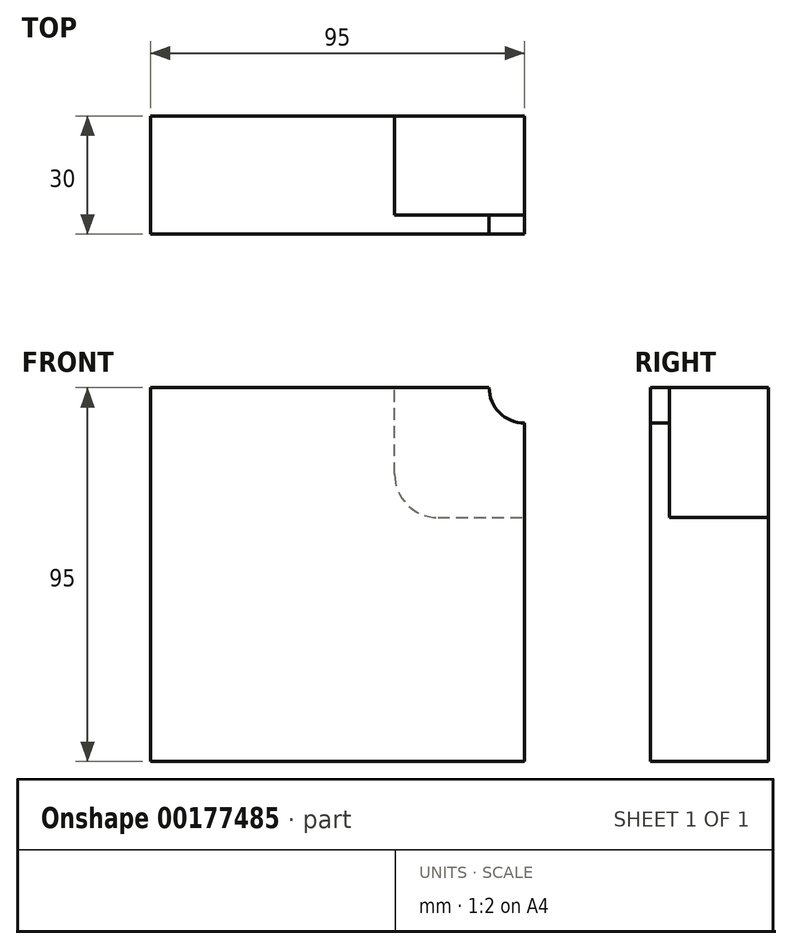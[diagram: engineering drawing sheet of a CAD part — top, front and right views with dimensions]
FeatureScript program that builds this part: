
annotation { "Feature Type Name" : "Feature", "Feature Type Description" : "" }
export const myFeature = defineFeature(function(context is Context, id is Id, definition is map)
    precondition{}
    {
        {
            var Q0;
            Q0=qCreatedBy(makeId("Front.planeOp"),FACE);
            var sketch = newSketch(context, id + "F0", { "sketchPlane" : qUnion([Q0])});
            skLineSegment(sketch, "E0.bottom", {"start": v(47.5, -47.5) * mm, "end": v(-47.5, -47.5) * mm});
            skLineSegment(sketch, "E0.top", {"start": v(47.5, 47.5) * mm, "end": v(-47.5, 47.5) * mm});
            skLineSegment(sketch, "E0.left", {"start": v(47.5, -47.5) * mm, "end": v(47.5, 47.5) * mm});
            skLineSegment(sketch, "E0.right", {"start": v(-47.5, -47.5) * mm, "end": v(-47.5, 47.5) * mm});
            skPoint(sketch, "E0.middle", {"position": v(0, 0) * mm});
            skSolve(sketch);
        }
        {
            var Q0;
            Q0 = qSketchRegion(id + "F0", true);
            extrude(context, id + "F1", {"entities" : qUnion([Q0]), "depth" : 30 * mm});
        }
        {
            var Q0;
            Q0=makeQuery(id+"F1.opExtrude","CAP_FACE",FACE,{"disambiguationData":[OSD([sQuery(id+"F0.wireOp",EDGE,"E0.bottom"),sQuery(id+"F0.wireOp",EDGE,"E0.top"),sQuery(id+"F0.wireOp",EDGE,"E0.left"),sQuery(id+"F0.wireOp",EDGE,"E0.right")])],"isStart":false});
            var sketch = newSketch(context, id + "F2", { "sketchPlane" : qUnion([Q0])});
            skCircle(sketch, "E1", {"center": v(47.5, 47.5) * mm, "radius": 9 * mm});
            skSolve(sketch);
        }
        {
            var Q0;
            Q0 = qSketchRegion(id + "F2", true);
            extrude(context, id + "F3", {"entities" : qUnion([Q0]), "operationType" : NewBodyOperationType.REMOVE, "oppositeDirection" : true, "depth" : 40 * mm});
        }
        {
            var Q0;
            Q0=makeQuery(id+"F1.opExtrude","CAP_FACE",FACE,{"disambiguationData":[OSD([sQuery(id+"F0.wireOp",EDGE,"E0.bottom"),sQuery(id+"F0.wireOp",EDGE,"E0.top"),sQuery(id+"F0.wireOp",EDGE,"E0.left"),sQuery(id+"F0.wireOp",EDGE,"E0.right")])],"isStart":true});
            var sketch = newSketch(context, id + "F4", { "sketchPlane" : qUnion([Q0])});
            skLineSegment(sketch, "E2.bottom", {"start": v(-14.5, 14.5) * mm, "end": v(-80.5, 14.5) * mm});
            skLineSegment(sketch, "E2.top", {"start": v(-14.5, 80.5) * mm, "end": v(-80.5, 80.5) * mm});
            skLineSegment(sketch, "E2.left", {"start": v(-14.5, 14.5) * mm, "end": v(-14.5, 80.5) * mm});
            skLineSegment(sketch, "E2.right", {"start": v(-80.5, 14.5) * mm, "end": v(-80.5, 80.5) * mm});
            skPoint(sketch, "E2.middle", {"position": v(-47.5, 47.5) * mm});
            skSolve(sketch);
        }
        {
            var Q0;
            Q0 = qSketchRegion(id + "F4", true);
            extrude(context, id + "F5", {"entities" : qUnion([Q0]), "operationType" : NewBodyOperationType.REMOVE, "oppositeDirection" : true, "depth" : 25.2 * mm});
        }
        {
            var Q0;
            Q0=makeQuery(id+"F5.boolean.opBoolean","COPY",EDGE,{"derivedFrom":makeQuery(id+"F5.opExtrude","SWEPT_EDGE",EDGE,{"disambiguationData":[OSD([sQuery(id+"F4.wireOp",EDGE,"E2.bottom"),sQuery(id+"F4.wireOp",EDGE,"E2.left")])]})});
            fillet(context, id + "F6", {"entities" : qUnion([Q0]), "radius" : 11 * mm, "tangentPropagation" : true, "allowEdgeOverflow" : false});
        }
    });
